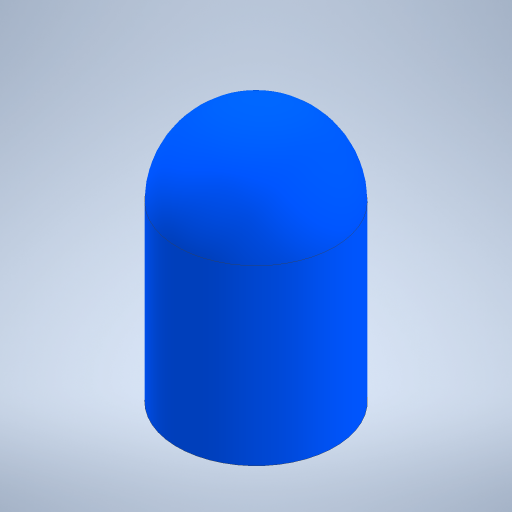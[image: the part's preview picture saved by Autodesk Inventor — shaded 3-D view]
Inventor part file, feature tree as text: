
AUTODESK INVENTOR PART (.ipt)
format: ipt  version: 2024.2 (Build 282272000, 272)  size: 238,592 bytes
history: native  units: mm
features: extrude x1, fillet x1, sketch x1
ambient origin geometry x8: Origin, YZ Plane, XZ Plane, XY Plane, X Axis, Y Axis, Z Axis, Center Point
bodies: Solid1 (feature_tree)
feature tree (3):
  extrude  "Extrusion1"  Depth=2.5mm TaperAngle=0.0deg
  fillet  "Fillet1"  Radius=2.5mm
  sketch  "Sketch1"  dims[d0=5.0mm d1=8.0mm d2=0.0mm d3=2.5mm]
